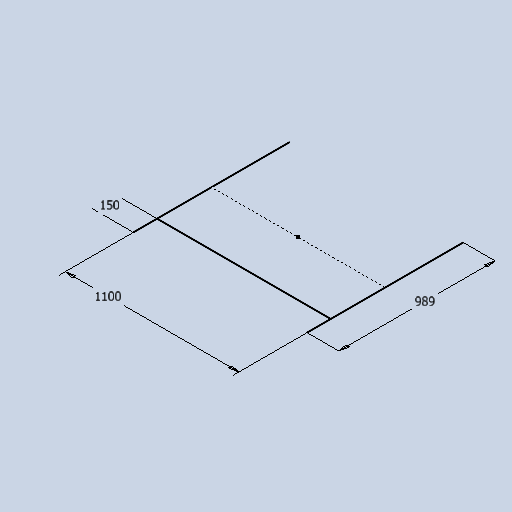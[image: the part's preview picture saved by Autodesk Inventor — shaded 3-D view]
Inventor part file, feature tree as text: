
AUTODESK INVENTOR PART (.ipt)
format: ipt  version: 2025 (Build 290162010, 162A)  size: 250,880 bytes
history: native  units: mm
features: sketch x1
ambient origin geometry x8: Origin, YZ Plane, XZ Plane, XY Plane, X Axis, Y Axis, Z Axis, Center Point
feature tree (1):
  sketch  "Sketch1"  dims[d0=989.0mm d1=1100.0mm d2=150.0mm]
